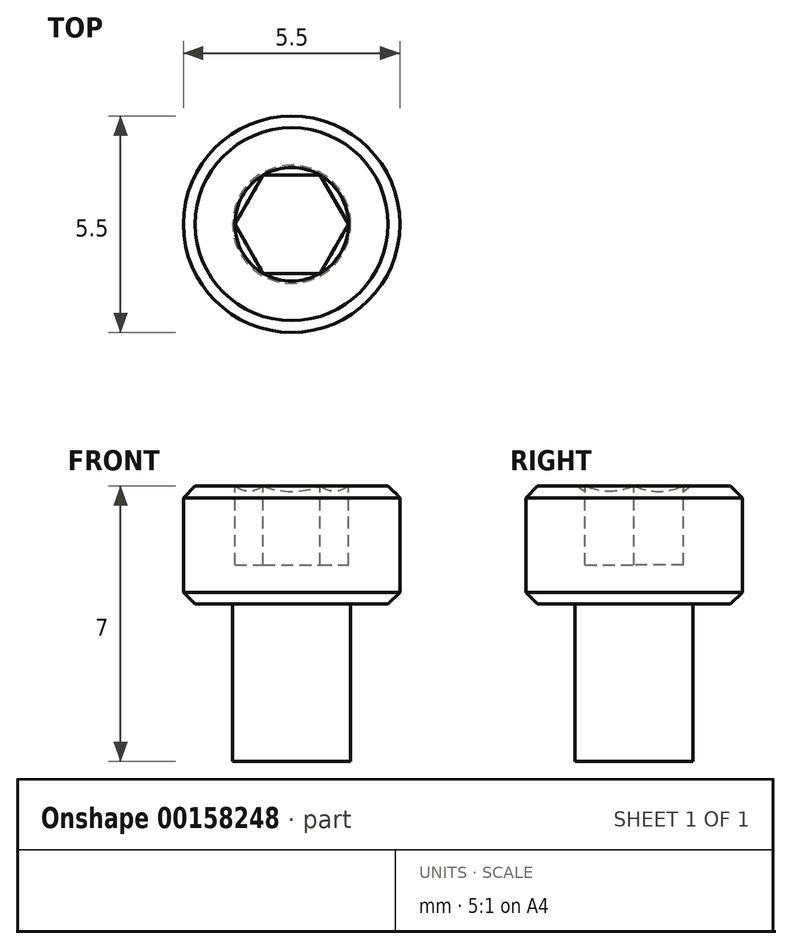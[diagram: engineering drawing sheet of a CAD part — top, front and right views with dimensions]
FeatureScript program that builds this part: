
annotation { "Feature Type Name" : "Feature", "Feature Type Description" : "" }
export const myFeature = defineFeature(function(context is Context, id is Id, definition is map)
    precondition{}
    {
        {
            var Q0;
            Q0=qCreatedBy(makeId("Front.planeOp"),FACE);
            var sketch = newSketch(context, id + "F0", { "sketchPlane" : qUnion([Q0])});
            skLineSegment(sketch, "E0", {"start": v(0, 3) * mm, "end": v(2.75, 3) * mm});
            skLineSegment(sketch, "E1", {"start": v(2.75, 3) * mm, "end": v(2.75, 0) * mm});
            skLineSegment(sketch, "E2", {"start": v(2.75, 0) * mm, "end": v(1.5, 0) * mm});
            skLineSegment(sketch, "E3", {"start": v(1.5, 0) * mm, "end": v(1.5, -4) * mm});
            skLineSegment(sketch, "E4", {"start": v(1.5, -4) * mm, "end": v(0, -4) * mm});
            skLineSegment(sketch, "E5", {"start": v(0, -4) * mm, "end": v(0, 3) * mm, "construction": true});
            skLineSegment(sketch, "E6", {"start": v(0, 3) * mm, "end": v(0, -4) * mm});
            skSolve(sketch);
        }
        {
            var Q0;
            Q0=makeQuery(id+"F0.imprint","IMPRINT",FACE,{"disambiguationData":[TD([[makeQuery(id+"F0.imprint","IMPRINT",EDGE,{"derivedFrom":sQuery(id+"F0.wireOp",EDGE,"E0")}),-1.0]])]});
            var Q1;
            Q1=sQuery(id+"F0.wireOp",EDGE,"E6");
            revolve(context, id + "F1", {"entities" : qUnion([Q0]), "axis" : qUnion([Q1]), "revolveType" : RevolveType.FULL});
        }
        {
            var Q0;
            Q0=makeQuery(id+"F1.opRevolve","SWEPT_FACE",FACE,{"disambiguationData":[OSD([sQuery(id+"F0.wireOp",EDGE,"E0")])]});
            var sketch = newSketch(context, id + "F2", { "sketchPlane" : qUnion([Q0])});
            skCircle(sketch, "E7.cCircle", {"center": v(0, 0) * mm, "radius": 1.25 * mm, "construction": true});
            skLineSegment(sketch, "E7.0", {"start": v(0.72, 1.25) * mm, "end": v(1.44, 0) * mm});
            skLineSegment(sketch, "E7.1", {"start": v(1.44, 0) * mm, "end": v(0.72, -1.25) * mm});
            skLineSegment(sketch, "E7.2", {"start": v(0.72, -1.25) * mm, "end": v(-0.72, -1.25) * mm});
            skLineSegment(sketch, "E7.3", {"start": v(-0.72, -1.25) * mm, "end": v(-1.44, 0) * mm});
            skLineSegment(sketch, "E7.4", {"start": v(-1.44, 0) * mm, "end": v(-0.72, 1.25) * mm});
            skLineSegment(sketch, "E7.5", {"start": v(-0.72, 1.25) * mm, "end": v(0.72, 1.25) * mm});
            skPoint(sketch, "E7.0.midPoint", {"position": v(1.08, 0.63) * mm});
            skSolve(sketch);
        }
        {
            var Q0;
            Q0=qSketchRegion(id+"F2",true);
            extrude(context, id + "F3", {"entities" : qUnion([Q0]), "operationType" : NewBodyOperationType.REMOVE, "oppositeDirection" : true, "depth" : 2 * mm});
        }
        {
            var Q0;
            Q0=qCreatedBy(makeId("Front.planeOp"),FACE);
            var sketch = newSketch(context, id + "F4", { "sketchPlane" : qUnion([Q0])});
            skArc(sketch, "E8", {"start": v(0, 7.17) * mm, "mid": v(-2.33, 4.83) * mm, "end": v(0, 2.5) * mm});
            skLineSegment(sketch, "E9", {"start": v(0, 4.83) * mm, "end": v(0, 0) * mm, "construction": true});
            skLineSegment(sketch, "E10", {"start": v(0, 7.17) * mm, "end": v(0, 2.5) * mm});
            skSolve(sketch);
        }
        {
            var Q0;
            Q0=qSketchRegion(id+"F4",true);
            var Q1;
            Q1=sQuery(id+"F4.wireOp",EDGE,"E9");
            revolve(context, id + "F5", {"operationType" : NewBodyOperationType.REMOVE, "entities" : qUnion([Q0]), "axis" : qUnion([Q1]), "revolveType" : RevolveType.FULL, "oppositeDirection" : true});
        }
        {
            var Q0;
            Q0=makeQuery(id+"F1.opRevolve","SWEPT_EDGE",EDGE,{"disambiguationData":[OSD([sQuery(id+"F0.wireOp",EDGE,"E0"),sQuery(id+"F0.wireOp",EDGE,"E1")])]});
            var Q1;
            Q1=makeQuery(id+"F1.opRevolve","SWEPT_EDGE",EDGE,{"disambiguationData":[OSD([sQuery(id+"F0.wireOp",EDGE,"E1"),sQuery(id+"F0.wireOp",EDGE,"E2")])]});
            chamfer(context, id + "F6", {"entities" : qUnion([Q0, Q1]), "width" : .3 * mm, "tangentPropagation" : true});
        }
    });
